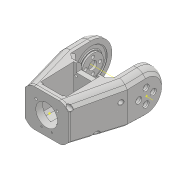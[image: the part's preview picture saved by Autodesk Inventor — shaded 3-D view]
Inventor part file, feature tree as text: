
AUTODESK INVENTOR PART (.ipt)
format: ipt  version: 2018 (Build 220112000, 112)  size: 1,154,048 bytes
history: native  units: mm
features: projected_geometry x49, sketch x46, extrude x38, hole x13, fillet x12, other x10, chamfer x6, reference x3, mirror x1, plane x1
ambient origin geometry x8: Origin, YZ Plane, XZ Plane, XY Plane, X Axis, Y Axis, Z Axis, Center Point
bodies: Solid1 (feature_tree)
feature tree (179):
  extrude  "Extrusion1"  Depth=45.0mm
  extrude  "Extrusion2"  Depth=2.25mm
  hole  "Hole1"  [1 undecoded]
  hole  "Hole2"  [1 undecoded]
  fillet  "Fillet1"  Radius=14.0mm
  extrude  "Extrusion3"  Depth=18.5mm
  extrude  "Extrusion4"  Depth=10.0mm
  extrude  "Extrusion5"  Depth=2.0mm
  extrude  "Extrusion6"  Depth=2.0mm
  hole  "Hole3"  [1 undecoded]
  extrude  "Extrusion7"  Depth=2.0mm
  extrude  "Extrusion8"  Depth=1.0mm TaperAngle=0.0deg
  extrude  "Extrusion9"  Depth=24.5mm
  extrude  "Extrusion10"  Depth=10.0mm
  extrude  "Extrusion11"  Depth=14.5mm
  extrude  "Extrusion13"  Depth=14.5mm
  extrude  "Extrusion14"  Depth=5.0mm
  extrude  "Extrusion15"  Depth=2.25mm
  extrude  "Extrusion16"  Depth=5.0mm
  extrude  "Extrusion17"  Depth=9.0mm
  chamfer  "Chamfer1"  Distance=1.0mm
  fillet  "Fillet7"  Radius=20.7mm
  fillet  "Fillet8"  Radius=32.0mm
  mirror  "Mirror1"
  sketch  "Sketch26"  dims[d55=2.25mm d56=5.0mm]
  extrude  "Extrusion24"  Depth=1.0mm TaperAngle=0.0deg
  extrude  "Extrusion25"  Depth=8.0mm
  extrude  "Extrusion26"  Depth=0.2mm TaperAngle=0.0deg
  extrude  "Extrusion27"  Depth=5.0mm TaperAngle=0.0deg
  other  "Work Axis1"
  plane  "Work Plane2"
  extrude  "Extrusion28"  Depth=0.2mm TaperAngle=0.0deg
  extrude  "Extrusion29"  Depth=2.0mm TaperAngle=45.0deg
  extrude  "Extrusion31"  Depth=0.5mm
  extrude  "Extrusion32"  Depth=36.0mm
  extrude  "Extrusion33"  Depth=60.0mm
  sketch  "Sketch41"  dims[d100=0.2mm d101=0.0mm d102=2.5mm d103=2.0mm d104=45.0deg]
  extrude  "Extrusion34"  Depth=2.3mm
  chamfer  "Chamfer6"  Distance=15.0mm
  fillet  "Fillet9"  Radius=15.0mm
  extrude  "Extrusion35"  Depth=15.0mm TaperAngle=0.0deg
  extrude  "Extrusion36"  Depth=41.5mm
  fillet  "Fillet10"  Radius=15.5mm
  extrude  "Extrusion37"  Depth=5.0mm
  extrude  "Extrusion38"  Depth=100.0mm TaperAngle=0.0deg
  extrude  "Extrusion39"  Depth=11.5mm
  extrude  "Extrusion40"  Depth=11.5mm
  hole  "Hole6"  [1 undecoded]
  fillet  "Fillet12"  Radius=100.0mm
  extrude  "Extrusion41"  Depth=100.0mm TaperAngle=0.0deg
  extrude  "Extrusion42"  Depth=2.0mm
  hole  "Hole7"  [1 undecoded]
  extrude  "Extrusion43"  Depth=1.0mm TaperAngle=0.0deg
  extrude  "Extrusion44"  Depth=2.0mm
  sketch  "Sketch58"  dims[d202=15.0deg d204=10.970628mm]
  hole  "Hole8"  [1 undecoded]
  hole  "Hole9"  [1 undecoded]
  hole  "Hole10"  [1 undecoded]
  hole  "Hole11"  [1 undecoded]
  hole  "Hole12"  [1 undecoded]
  hole  "Hole13"  [1 undecoded]
  hole  "Hole14"  [1 undecoded]
  hole  "Hole15"  [1 undecoded]
  chamfer  "Chamfer10"  Distance=0.75mm
  chamfer  "Chamfer11"  Distance=20.5mm
  chamfer  "Chamfer12"  Distance=3.05mm
  chamfer  "Chamfer13"  Distance=14.0mm
  extrude  "Extrusion45"  Depth=0.6mm
  fillet  "Fillet13"  Radius=1.55mm
  extrude  "Extrusion46"  Depth=0.6mm
  fillet  "Fillet14"  Radius=2.5mm
  fillet  "Fillet15"  Radius=8.0mm
  fillet  "Fillet16"  Radius=2.5mm
  fillet  "Fillet17"  Radius=4.624622mm
  fillet  "Fillet18"  Radius=4.624622mm
  sketch  "Sketch1"  dims[d0=24.5mm d1=45.0mm]
  sketch  "Sketch2"  dims[d2=1.95mm d3=0.0mm d4=2.25mm]
  projected_geometry  "Projected Loop1"
  sketch  "Sketch3"  dims[d5=20.0mm d6=2.25mm]
  projected_geometry  "Projected Loop2"
  sketch  "Sketch4"  dims[d7=5.25mm d8=5.25mm d9=14.0mm]
  projected_geometry  "Projected Loop3"
  sketch  "Sketch5"  dims[d10=5.25mm d11=18.5mm]
  projected_geometry  "Projected Loop4"
  sketch  "Sketch6"  dims[d12=10.0mm d13=0.0mm d14=20.5mm]
  projected_geometry  "Projected Loop5"
  sketch  "Sketch7"  dims[d15=2.0mm d16=2.195mm]
  projected_geometry  "Projected Loop6"
  sketch  "Sketch8"  dims[d17=2.0mm]
  projected_geometry  "Projected Loop7"
  sketch  "Sketch9"  dims[d18=2.4mm d19=6.0mm d20=4.4mm d21=2.0mm d22=90.0deg d23=8.0mm d24=20.594885mm d25=20.5mm]
  projected_geometry  "Projected Loop8"
  projected_geometry  "Projected Loop9"
  sketch  "Sketch10"  dims[d26=26.65mm d27=2.0mm]
  projected_geometry  "Projected Loop10"
  projected_geometry  "Projected Loop11"
  sketch  "Sketch11"  dims[d28=2.0mm]
  projected_geometry  "Projected Loop12"
  sketch  "Sketch12"  dims[d29=2.4mm d30=6.0mm d31=4.4mm d32=2.0mm d33=90.0deg d34=8.0mm d35=20.594885mm d36=0.5mm]
  sketch  "Sketch13"  dims[d37=18.0mm d38=1.0mm d39=0.0mm]
  sketch  "Sketch14"  dims[d41=5.0mm d42=0.0mm d43=24.5mm]
  projected_geometry  "Projected Loop13"
  sketch  "Sketch16"  dims[d44=1.15mm d45=0.0mm d46=10.0mm]
  projected_geometry  "Projected Loop14"
  sketch  "Sketch17"  dims[d47=21.0mm d48=14.5mm]
  projected_geometry  "Projected Loop15"
  sketch  "Sketch18"  dims[d49=20.0mm d50=14.5mm]
  projected_geometry  "Projected Loop16"
  sketch  "Sketch19"  dims[d51=24.5mm d52=5.0mm]
  projected_geometry  "Projected Loop17"
  sketch  "Sketch20"  dims[d53=5.0mm d54=2.25mm]
  projected_geometry  "Projected Loop18"
  projected_geometry  "Projected Loop25"
  sketch  "Sketch31"  dims[d57=5.0mm d58=9.0mm]
  projected_geometry  "Projected Loop30"
  reference  "Reference1"
  sketch  "Sketch32"  dims[d59=14.75mm]
  projected_geometry  "Projected Loop31"
  sketch  "Sketch33"  dims[d60=4.0mm d61=1.0mm d62=0.0mm d63=20.7mm]
  projected_geometry  "Projected Loop32"
  sketch  "Sketch34"  dims[d64=2.3mm d65=6.0mm d66=4.4mm d67=2.0mm d68=90.0deg d69=8.0mm d70=20.594885mm d72=32.0mm]
  projected_geometry  "Projected Loop33"
  other  "Work Point1"
  other  "Work Point2"
  other  "Work Point3"
  sketch  "Sketch35"  dims[d73=3.0mm d74=0.0mm d75=1.0mm d76=0.0mm]
  sketch  "Sketch37"  dims[d77=12.25mm d78=0.0mm d80=8.0mm]
  projected_geometry  "Projected Loop34"
  sketch  "Sketch38"  dims[d81=4.5mm d82=0.0mm d84=0.2mm d85=0.0mm]
  sketch  "Sketch39"  dims[d91=8.0mm d92=0.0mm d93=5.0mm d94=0.0mm]
  sketch  "Sketch40"  dims[d95=5.0mm d96=0.0mm d98=0.2mm d99=0.0mm]
  projected_geometry  "Projected Loop35"
  projected_geometry  "Projected Loop36"
  projected_geometry  "Projected Loop37"
  projected_geometry  "Projected Loop38"
  sketch  "Sketch42"  dims[d105=1.5mm d114=0.5mm]
  projected_geometry  "Projected Loop39"
  sketch  "Sketch43"  dims[d130=60.0mm d131=36.0mm]
  reference  "Reference2"
  reference  "Reference3"
  sketch  "Sketch45"  dims[d146=40.0mm d147=60.0mm]
  projected_geometry  "Projected Loop40"
  sketch  "Sketch46"  dims[d148=0.0mm d149=2.3mm d150=15.0mm d151=0.0mm d152=15.0mm d153=0.0mm]
  projected_geometry  "Projected Loop41"
  sketch  "Sketch48"  dims[d154=15.0mm d155=0.0mm d156=15.0mm d157=0.0mm]
  projected_geometry  "Projected Loop43"
  sketch  "Sketch49"  dims[d158=20.5mm d159=41.5mm d160=15.5mm]
  projected_geometry  "Projected Loop44"
  projected_geometry  "Projected Loop45"
  sketch  "Sketch50"  dims[d161=15.5mm d162=5.0mm]
  projected_geometry  "Projected Loop46"
  sketch  "Sketch52"  dims[d165=100.0mm d166=0.0mm d167=100.0mm d168=0.0mm]
  sketch  "Sketch53"  dims[d172=0.0mm d173=11.5mm]
  projected_geometry  "Projected Loop47"
  sketch  "Sketch54"  dims[d175=11.5mm d176=11.5mm]
  projected_geometry  "Projected Loop48"
  sketch  "Sketch55"  dims[d179=100.0mm d180=0.0mm d187=7.0mm d188=100.0mm d189=0.0mm]
  sketch  "Sketch56"  dims[d193=100.0mm d194=0.0mm d195=100.0mm d196=0.0mm]
  projected_geometry  "Projected Loop49"
  sketch  "Sketch57"  dims[d197=5.0mm d198=2.0mm d199=45.0deg d200=8.0mm]
  projected_geometry  "Projected Loop50"
  projected_geometry  "Projected Loop51"
  projected_geometry  "Projected Loop52"
  projected_geometry  "Projected Loop53"
  projected_geometry  "Projected Loop55"
  projected_geometry  "Projected Loop56"
  projected_geometry  "Projected Loop57"
  sketch  "Sketch59"  dims[d205=15.470628mm d206=1.0mm d207=0.0mm]
  projected_geometry  "Projected Loop58"
  sketch  "Sketch60"  dims[d208=1.0mm d209=0.0mm d213=2.0mm d215=15.0deg d216=4.0mm d217=4.0mm d218=5.0mm d219=0.0mm d222=32.0mm d223=4.0mm d224=0.0mm d225=2.5mm d226=0.0mm d227=6.5mm d228=0.0mm d235=1.567mm d236=15.0mm d237=4.0mm d238=2.0mm d239=90.0deg d240=15.0mm d241=20.594885mm d243=0.75mm d244=20.5mm d245=3.05mm d246=0.0mm d247=14.0mm d248=3.2mm d249=6.0mm d250=4.0mm d251=2.0mm d252=90.0deg d253=8.8mm d254=20.594885mm d255=20.5mm d256=1.55mm d257=0.0mm d258=8.0mm d259=2.5mm d260=0.0mm d261=8.0mm d262=2.5mm d263=0.0mm d266=4.624622mm d267=4.624622mm d268=2.75mm d269=2.75mm d270=2.35mm d271=2.35mm d272=14.0mm d273=4.0mm d274=5.6mm d275=3.708mm d276=3.023mm d277=2.0mm d278=14.3117mm d279=17.0mm d280=0.0mm d281=4.0mm d282=3.708mm d283=3.023mm d284=2.0mm d285=14.3117mm d286=19.0mm d287=0.0mm d288=4.0mm d289=3.708mm d290=3.023mm d291=2.0mm d292=14.3117mm d293=20.0mm d294=0.0mm d295=2.3mm d296=4.0mm d297=4.4mm d298=2.0mm d299=90.0deg d300=32.25mm d301=0.0mm d302=3.3mm d303=4.0mm d304=6.3mm d305=2.0mm d306=90.0deg d307=32.25mm d308=0.0mm d309=1.567mm d310=4.0mm d311=6.3mm d312=2.0mm d313=90.0deg d314=45.0mm d315=20.594885mm d316=1.567mm d317=4.0mm d318=6.3mm d319=2.0mm d320=90.0deg d321=55.0mm d322=20.594885mm d323=2.459mm d324=6.0mm d325=6.3mm d326=2.0mm d327=90.0deg d328=50.0mm d329=20.594885mm d330=3.0mm d331=2.0mm d332=45.0deg d333=5.0mm d334=20.0mm d335=45.0deg d336=5.0mm d337=20.0mm d338=45.0deg d339=5.0mm d340=20.0mm d341=45.0deg d342=6.0mm d343=6.0mm d344=6.0mm d345=6.0mm d346=2.0mm d347=0.0mm d348=1.5mm d349=6.0mm d350=6.0mm d351=6.0mm d352=6.0mm d353=3.0mm d354=0.0mm d355=1.5mm d356=0.4mm d357=0.4mm d358=0.3mm d359=1.0mm d360=0.6mm]
  projected_geometry  "Projected Loop59"
  parser-record x1  (decoder bookkeeping rows leaked as tree rows — omitted from the tree; the rows remain in map.json)
  other  "servocheck.iam"
  other  "LX-16A:3"
  other  "DUOPAN-SG-SJ_10"
  projected_geometry  "Project Cut Edges1"
  projected_geometry  "Project Cut Edges3"
  other  "bottomarm:1"
  other  "arm1:1"
note: 13 required parameter values undecoded (feature->parameter linkage not recoverable at this tier; creation-order binding heuristic only, values carry confidence <= 0.55)
note: 1 file-system path scrubbed to <path> (originals preserved in map.json)
